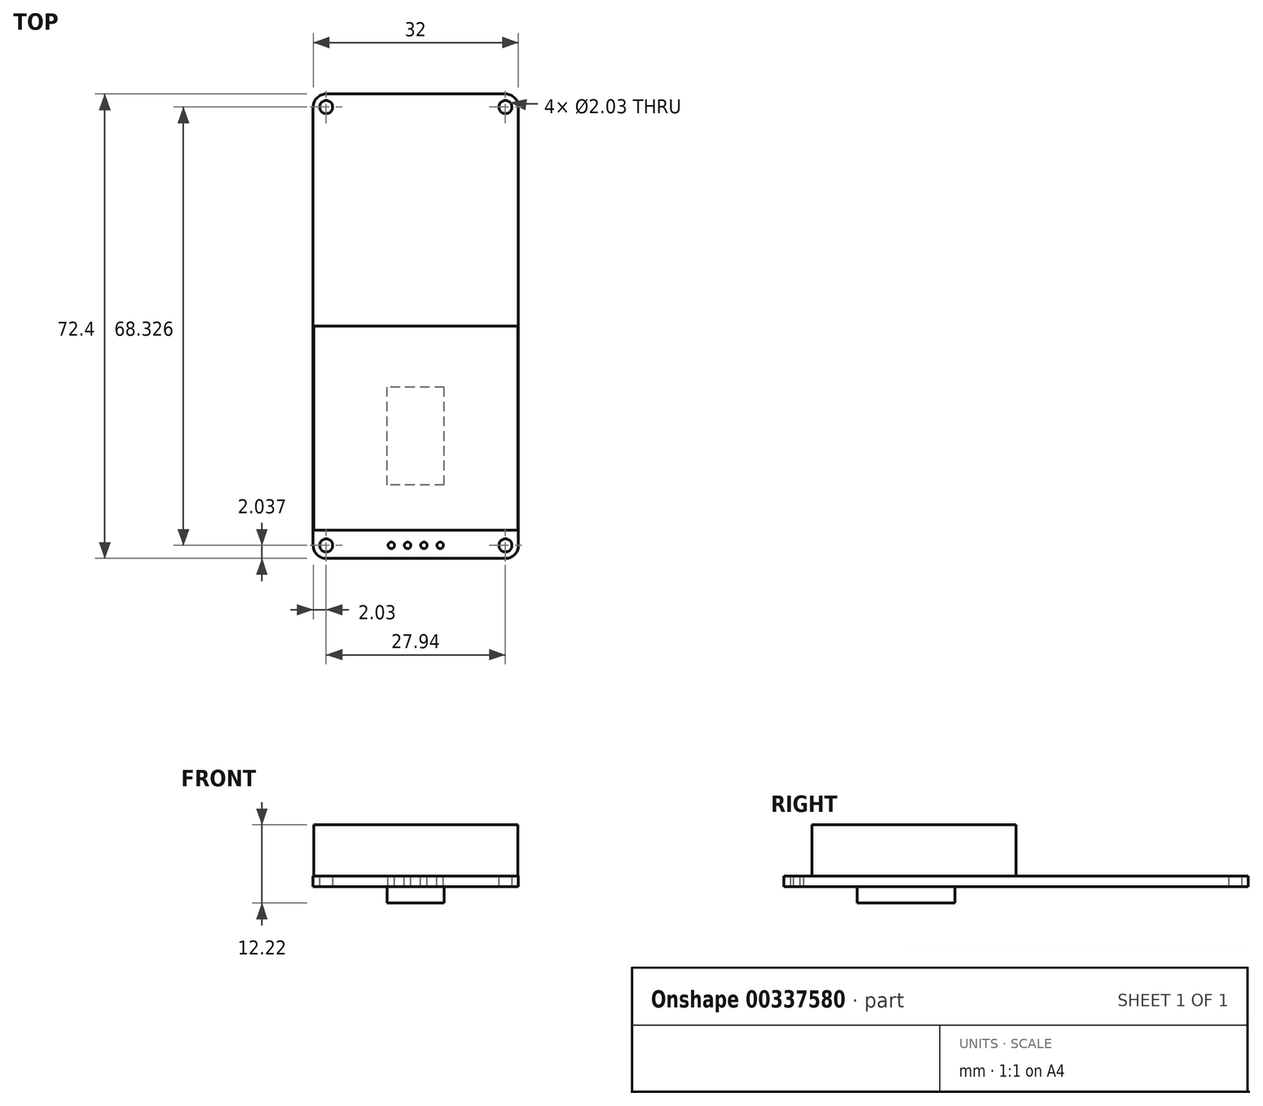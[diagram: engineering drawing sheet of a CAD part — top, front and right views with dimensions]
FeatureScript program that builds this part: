
annotation { "Feature Type Name" : "Feature", "Feature Type Description" : "" }
export const myFeature = defineFeature(function(context is Context, id is Id, definition is map)
    precondition{}
    {
        {
            var Q0;
            Q0=qCreatedBy(makeId("Top.planeOp"),FACE);
            var sketch = newSketch(context, id + "F0", { "sketchPlane" : qUnion([Q0])});
            skLineSegment(sketch, "E0.bottom", {"start": v(16, 36.2) * mm, "end": v(-16, 36.2) * mm});
            skLineSegment(sketch, "E0.top", {"start": v(16, -36.2) * mm, "end": v(-16, -36.2) * mm});
            skLineSegment(sketch, "E0.left", {"start": v(16, 36.2) * mm, "end": v(16, -36.2) * mm});
            skLineSegment(sketch, "E0.right", {"start": v(-16, 36.2) * mm, "end": v(-16, -36.2) * mm});
            skPoint(sketch, "E0.middle", {"position": v(0, 0) * mm});
            skLineSegment(sketch, "E1.bottom", {"start": v(13.97, 34.16) * mm, "end": v(-13.97, 34.16) * mm, "construction": true});
            skLineSegment(sketch, "E1.top", {"start": v(13.97, -34.16) * mm, "end": v(-13.97, -34.16) * mm, "construction": true});
            skLineSegment(sketch, "E1.left", {"start": v(13.97, 34.16) * mm, "end": v(13.97, -34.16) * mm, "construction": true});
            skLineSegment(sketch, "E1.right", {"start": v(-13.97, 34.16) * mm, "end": v(-13.97, -34.16) * mm, "construction": true});
            skCircle(sketch, "E2", {"center": v(13.97, 34.16) * mm, "radius": 1.02 * mm});
            skCircle(sketch, "E3", {"center": v(-13.97, 34.16) * mm, "radius": 1.02 * mm});
            skCircle(sketch, "E4", {"center": v(-13.97, -34.16) * mm, "radius": 1.02 * mm});
            skCircle(sketch, "E5", {"center": v(13.97, -34.16) * mm, "radius": 1.02 * mm});
            skSolve(sketch);
        }
        {
            var Q0;
            Q0=makeQuery(id+"F0.imprint","IMPRINT",FACE,{"disambiguationData":[TD([[makeQuery(id+"F0.imprint","IMPRINT",EDGE,{"derivedFrom":sQuery(id+"F0.wireOp",EDGE,"E0.bottom")}),1.0]])]});
            extrude(context, id + "F1", {"entities" : qUnion([Q0]), "depth" : 1.65 * mm});
        }
        {
            var Q0;
            Q0=makeQuery(id+"F1.opExtrude","CAP_FACE",FACE,{"disambiguationData":[OSD([sQuery(id+"F0.wireOp",EDGE,"E0.bottom"),sQuery(id+"F0.wireOp",EDGE,"E0.top"),sQuery(id+"F0.wireOp",EDGE,"E0.left"),sQuery(id+"F0.wireOp",EDGE,"E0.right"),sQuery(id+"F0.wireOp",EDGE,"E2"),sQuery(id+"F0.wireOp",EDGE,"E3"),sQuery(id+"F0.wireOp",EDGE,"E4"),sQuery(id+"F0.wireOp",EDGE,"E5")])],"isStart":false});
            var sketch = newSketch(context, id + "F2", { "sketchPlane" : qUnion([Q0])});
            skLineSegment(sketch, "E6.bottom", {"start": v(15.9, 0) * mm, "end": v(-15.9, 0) * mm});
            skLineSegment(sketch, "E6.top", {"start": v(15.9, -31.8) * mm, "end": v(-15.9, -31.8) * mm});
            skLineSegment(sketch, "E6.left", {"start": v(15.9, 0) * mm, "end": v(15.9, -31.8) * mm});
            skLineSegment(sketch, "E6.right", {"start": v(-15.9, 0) * mm, "end": v(-15.9, -31.8) * mm});
            skPoint(sketch, "E6.middle", {"position": v(0, -15.9) * mm});
            skSolve(sketch);
        }
        {
            var Q0;
            Q0 = qSketchRegion(id + "F2", true);
            extrude(context, id + "F3", {"entities" : qUnion([Q0]), "depth" : 8.03 * mm});
        }
        {
            var Q0;
            Q0=makeQuery(id+"F1.opExtrude","SWEPT_EDGE",EDGE,{"disambiguationData":[OSD([sQuery(id+"F0.wireOp",EDGE,"E0.top"),sQuery(id+"F0.wireOp",EDGE,"E0.left")])]});
            var Q1;
            Q1=makeQuery(id+"F1.opExtrude","SWEPT_EDGE",EDGE,{"disambiguationData":[OSD([sQuery(id+"F0.wireOp",EDGE,"E0.top"),sQuery(id+"F0.wireOp",EDGE,"E0.right")])]});
            var Q2;
            Q2=makeQuery(id+"F1.opExtrude","SWEPT_EDGE",EDGE,{"disambiguationData":[OSD([sQuery(id+"F0.wireOp",EDGE,"E0.bottom"),sQuery(id+"F0.wireOp",EDGE,"E0.right")])]});
            var Q3;
            Q3=makeQuery(id+"F1.opExtrude","SWEPT_EDGE",EDGE,{"disambiguationData":[OSD([sQuery(id+"F0.wireOp",EDGE,"E0.bottom"),sQuery(id+"F0.wireOp",EDGE,"E0.left")])]});
            fillet(context, id + "F4", {"entities" : qUnion([Q0, Q1, Q2, Q3]), "radius" : 2.03 * mm, "tangentPropagation" : true, "allowEdgeOverflow" : false});
        }
        {
            var Q0;
            Q0=makeQuery(id+"F1.opExtrude","CAP_FACE",FACE,{"disambiguationData":[OSD([sQuery(id+"F0.wireOp",EDGE,"E0.bottom"),sQuery(id+"F0.wireOp",EDGE,"E0.top"),sQuery(id+"F0.wireOp",EDGE,"E0.left"),sQuery(id+"F0.wireOp",EDGE,"E0.right"),sQuery(id+"F0.wireOp",EDGE,"E2"),sQuery(id+"F0.wireOp",EDGE,"E3"),sQuery(id+"F0.wireOp",EDGE,"E4"),sQuery(id+"F0.wireOp",EDGE,"E5")])],"isStart":false});
            var sketch = newSketch(context, id + "F5", { "sketchPlane" : qUnion([Q0])});
            skLineSegment(sketch, "E7", {"start": v(-13.97, -34.16) * mm, "end": v(-3.81, -34.16) * mm, "construction": true});
            skLineSegment(sketch, "E8", {"start": v(-3.81, -34.16) * mm, "end": v(-1.27, -34.16) * mm, "construction": true});
            skLineSegment(sketch, "E9", {"start": v(-1.27, -34.16) * mm, "end": v(1.27, -34.16) * mm, "construction": true});
            skLineSegment(sketch, "E10", {"start": v(1.27, -34.16) * mm, "end": v(3.8, -34.16) * mm, "construction": true});
            skLineSegment(sketch, "E11", {"start": v(3.8, -34.16) * mm, "end": v(13.97, -34.16) * mm, "construction": true});
            skCircle(sketch, "E12", {"center": v(3.8, -34.16) * mm, "radius": 0.5 * mm});
            skCircle(sketch, "E13", {"center": v(1.27, -34.16) * mm, "radius": 0.5 * mm});
            skCircle(sketch, "E14", {"center": v(-1.27, -34.16) * mm, "radius": 0.5 * mm});
            skCircle(sketch, "E15", {"center": v(-3.81, -34.16) * mm, "radius": 0.5 * mm});
            skSolve(sketch);
        }
        {
            var Q0;
            Q0 = qSketchRegion(id + "F5", true);
            extrude(context, id + "F6", {"entities" : qUnion([Q0]), "operationType" : NewBodyOperationType.REMOVE, "endBound" : BoundingType.THROUGH_ALL, "oppositeDirection" : true, "depth" : 25.4 * mm});
        }
        {
            var Q0;
            Q0=makeQuery(id+"F1.opExtrude","CAP_FACE",FACE,{"disambiguationData":[OSD([sQuery(id+"F0.wireOp",EDGE,"E0.bottom"),sQuery(id+"F0.wireOp",EDGE,"E0.top"),sQuery(id+"F0.wireOp",EDGE,"E0.left"),sQuery(id+"F0.wireOp",EDGE,"E0.right"),sQuery(id+"F0.wireOp",EDGE,"E2"),sQuery(id+"F0.wireOp",EDGE,"E3"),sQuery(id+"F0.wireOp",EDGE,"E4"),sQuery(id+"F0.wireOp",EDGE,"E5")])],"isStart":true});
            var sketch = newSketch(context, id + "F7", { "sketchPlane" : qUnion([Q0])});
            skLineSegment(sketch, "E16.bottom", {"start": v(4.44, 24.77) * mm, "end": v(-4.45, 24.77) * mm});
            skLineSegment(sketch, "E16.top", {"start": v(4.45, 9.52) * mm, "end": v(-4.44, 9.52) * mm});
            skLineSegment(sketch, "E16.left", {"start": v(4.45, 24.77) * mm, "end": v(4.44, 9.52) * mm});
            skLineSegment(sketch, "E16.right", {"start": v(-4.45, 24.77) * mm, "end": v(-4.44, 9.52) * mm});
            skPoint(sketch, "E16.middle", {"position": v(0, 17.14) * mm});
            skSolve(sketch);
        }
        {
            var Q0;
            Q0 = qSketchRegion(id + "F7", true);
            extrude(context, id + "F8", {"entities" : qUnion([Q0]), "operationType" : NewBodyOperationType.ADD, "depth" : 2.54 * mm});
        }
    });
